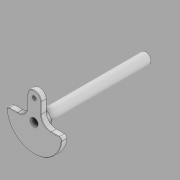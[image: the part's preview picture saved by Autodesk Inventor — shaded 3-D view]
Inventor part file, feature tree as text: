
AUTODESK INVENTOR PART (.ipt)
format: ipt  version: 2020 (Build 240168000, 168)  size: 155,136 bytes
history: native  units: in
note: dims shown in document units (in); Inventor stores cm internally (conversion verified against a paired STEP export)
features: sketch x4, extrude x3, other x1, hole x1, fillet x1
ambient origin geometry x8: Origin, YZ Plane, XZ Plane, XY Plane, X Axis, Y Axis, Z Axis, Center Point
bodies: Body1 (feature_tree)
feature tree (10):
  other  "Sólido1"
  extrude  "Extrusión1"  Depth=0.1875in
  hole  "Agujero1"  [1 undecoded]
  extrude  "Extrusión2"  Depth=0.5in
  extrude  "Extrusión3"  Depth=0.5in
  fillet  "Empalme1"  [1 undecoded]
  sketch  "Boceto1"  dims[d0=1.3125in d1=0.1875in]
  sketch  "Boceto2"  dims[d2=0.3182in d3=0.4773in]
  sketch  "Boceto3"  dims[d5=0.5in d6=0.1193in]
  sketch  "Boceto4"  dims[d7=0.125in d8=0.0in d9=0.5in d10=90.0deg d11=0.0979in d12=0.25in d13=0.375in d14=0.25in d15=0.5635in d16=1.0in d17=0.8108in d18=0.375in d19=0.1875in d20=0.0938in d21=0.0in d22=0.25in d23=2.4375in d24=0.0in d25=0.01in]
note: 2 required parameter values undecoded (feature->parameter linkage not recoverable at this tier; creation-order binding heuristic only, values carry confidence <= 0.55)
